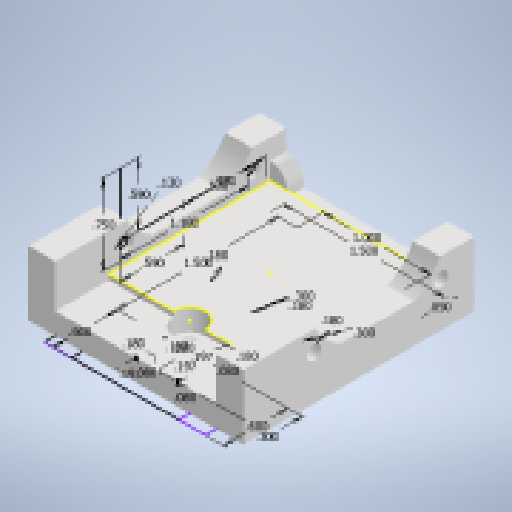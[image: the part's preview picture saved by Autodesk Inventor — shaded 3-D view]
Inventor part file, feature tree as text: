
AUTODESK INVENTOR PART (.ipt)
format: ipt  version: 2025.2 (Build 292293000, 293)  size: 529,408 bytes
history: native  units: in
note: dims shown in document units (in); Inventor stores cm internally (conversion verified against a paired STEP export)
features: sketch x15, extrude x13, thicken_offset x6, move_body x5, direct_edit x4, projected_geometry x2
ambient origin geometry x8: Origin, YZ Plane, XZ Plane, XY Plane, X Axis, Y Axis, Z Axis, Center Point
bodies: Solid1 (feature_tree)
feature tree (45):
  sketch  "Sketch1"  dims[d0=1.5in d1=1.0in]
  extrude  "Extrusion1"  Depth=1.5in
  extrude  "Extrusion2"  Depth=0.6in
  extrude  "Extrusion3"  Depth=1.5in
  extrude  "Extrusion4"  Depth=0.18in
  sketch  "Sketch3"  dims[d4=1.5in d5=0.18in]
  extrude  "Extrusion5"  Depth=0.05in
  sketch  "Sketch4"  dims[d6=0.18in d7=0.18in]
  extrude  "Extrusion6"  Depth=0.6in
  extrude  "Extrusion7"  Depth=0.3in
  extrude  "Extrusion8"  Depth=0.2in TaperAngle=0.0deg
  extrude  "Extrusion9"  Depth=0.2in TaperAngle=0.0deg
  thicken_offset  "Thicken1"
  thicken_offset  "Thicken2"
  thicken_offset  "Thicken3"
  thicken_offset  "Thicken4"
  thicken_offset  "Thicken5"
  thicken_offset  "Thicken6"
  extrude  "Extrusion10"  Depth=0.197in
  sketch  "Sketch10"  dims[d22=0.197in d23=0.197in]
  direct_edit  "Direct Edit1"
  sketch  "Sketch11"  dims[d24=0.08in d25=0.08in]
  extrude  "Extrusion11"  Depth=0.08in
  direct_edit  "Direct Edit2"
  extrude  "Extrusion12"  Depth=0.175in
  extrude  "Extrusion13"  Depth=0.4in
  direct_edit  "Direct Edit3"
  direct_edit  "Direct Edit4"
  sketch  "Sketch15"  dims[d33=1.0in d34=0.0in d35=0.05in d36=0.05in d37=1.55in d38=0.6in d39=0.0in d40=0.75in d41=0.59in d42=0.75in d43=0.59in d44=0.13in d45=1.18in d46=0.13in d47=2.0in d48=0.0in d49=0.25in d50=0.25in d51=2.0in d52=0.0in d53=0.2in d54=0.1in d55=0.2in d56=0.2in d57=0.3in d58=0.2in d59=0.3in d60=0.2in d61=0.1in d62=0.1in d63=0.2in d64=0.2in d66=1.75in d67=0.0in d68=0.0in d69=0.0in d70=-0.05in d71=0.0in d72=0.0in d73=-0.05in d74=0.197in d75=0.197in d76=0.08in d77=0.08in d78=0.16in d79=0.16in d80=0.16in d81=0.16in d82=0.16in d83=0.0in d84=0.0in d85=0.0in d86=-0.25in d87=0.24in d88=0.15in d89=0.5in d90=0.24in d91=0.5in d92=2.0in d93=0.0in d94=0.05in d95=0.0in d96=0.0in d97=0.0in d98=-0.01in d99=0.0in d100=0.0in d101=0.01in]
  sketch  "Sketch2"  dims[d2=0.18in d3=0.6in]
  sketch  "Sketch5"  dims[d8=0.25in d9=0.0in d10=0.05in]
  sketch  "Sketch6"  dims[d11=0.5in d12=0.0in d13=0.6in]
  sketch  "Sketch7"  dims[d14=0.3in d15=0.3in]
  sketch  "Sketch8"  dims[d16=0.3in d17=0.2in d18=0.0in]
  sketch  "Sketch9"  dims[d19=0.3in d20=0.2in d21=0.0in]
  sketch  "Sketch12"  dims[d26=0.175in d27=0.0in d28=0.18in]
  sketch  "Sketch13"  dims[d30=0.4in d31=0.4in]
  sketch  "Sketch14"  dims[d32=0.25in]
  projected_geometry  "Projected Loop1"
  projected_geometry  "Projected Loop2"
  move_body  "Move1"
  move_body  "Move2"
  move_body  "Move3"
  move_body  "Move4"
  move_body  "Move5"
